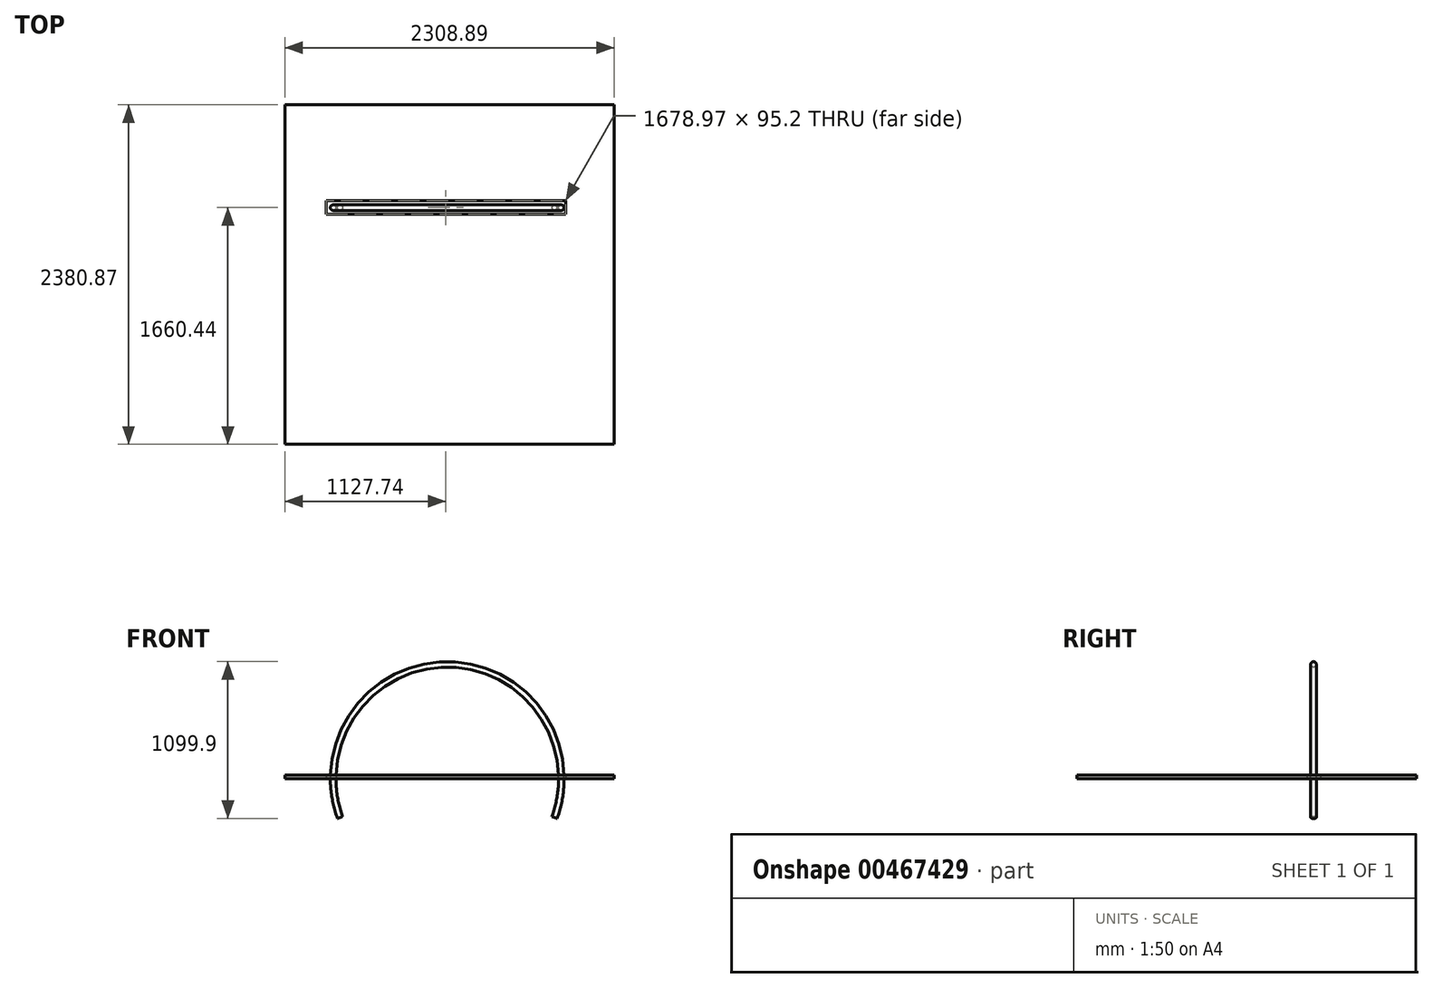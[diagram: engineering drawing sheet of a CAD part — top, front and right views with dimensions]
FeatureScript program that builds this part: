
annotation { "Feature Type Name" : "Feature", "Feature Type Description" : "" }
export const myFeature = defineFeature(function(context is Context, id is Id, definition is map)
    precondition{}
    {
        {
            var Q0;
            Q0=qCreatedBy(makeId("Top.planeOp"),FACE);
            var sketch = newSketch(context, id + "F0", { "sketchPlane" : qUnion([Q0])});
            skLineSegment(sketch, "E0", {"start": v(0, 0) * mm, "end": v(800.15, 0) * mm});
            skCircle(sketch, "E1", {"center": v(800.15, 0) * mm, "radius": 19.43 * mm});
            skLineSegment(sketch, "E2", {"start": v(0, 18.17) * mm, "end": v(0, -26.19) * mm});
            skSolve(sketch);
        }
        {
            var Q0;
            Q0=makeQuery(id+"F0.imprint","IMPRINT",FACE,{"disambiguationData":[TD([[makeQuery(id+"F0.imprint","IMPRINT",EDGE,{"derivedFrom":sQuery(id+"F0.wireOp",EDGE,"E1")}),1.0]])]});
            var Q1;
            Q1=sQuery(id+"F0.wireOp",EDGE,"E2");
            revolve(context, id + "F1", {"entities" : qUnion([Q0]), "axis" : qUnion([Q1]), "revolveType" : RevolveType.TWO_DIRECTIONS, "oppositeDirection" : true, "angle" : 20 * degree, "angleBack" : 160 * degree});
        }
        {
            var Q0;
            Q0=qCreatedBy(makeId("Top.planeOp"),FACE);
            var sketch = newSketch(context, id + "F2", { "sketchPlane" : qUnion([Q0])});
            skLineSegment(sketch, "E3.bottom", {"start": v(-1138.18, -1659.39) * mm, "end": v(1170.71, -1659.39) * mm});
            skLineSegment(sketch, "E3.top", {"start": v(-1138.18, 721.48) * mm, "end": v(1170.71, 721.48) * mm});
            skLineSegment(sketch, "E3.left", {"start": v(-1138.18, -1659.39) * mm, "end": v(-1138.18, 721.48) * mm});
            skLineSegment(sketch, "E3.right", {"start": v(1170.71, -1659.39) * mm, "end": v(1170.71, 721.48) * mm});
            skLineSegment(sketch, "E4.bottom", {"start": v(-849.92, 48.65) * mm, "end": v(829.04, 48.65) * mm});
            skLineSegment(sketch, "E4.top", {"start": v(-849.92, -46.55) * mm, "end": v(829.04, -46.55) * mm});
            skLineSegment(sketch, "E4.left", {"start": v(-849.92, 48.65) * mm, "end": v(-849.92, -46.55) * mm});
            skLineSegment(sketch, "E4.right", {"start": v(829.04, 48.65) * mm, "end": v(829.04, -46.55) * mm});
            skSolve(sketch);
        }
        {
            var Q0;
            Q0=makeQuery(id+"F2.imprint","IMPRINT",FACE,{"disambiguationData":[TD([[makeQuery(id+"F2.imprint","IMPRINT",EDGE,{"derivedFrom":sQuery(id+"F2.wireOp",EDGE,"E3.bottom")}),1.0]])]});
            extrude(context, id + "F3", {"entities" : qUnion([Q0]), "depth" : 25 * mm});
        }
    });
